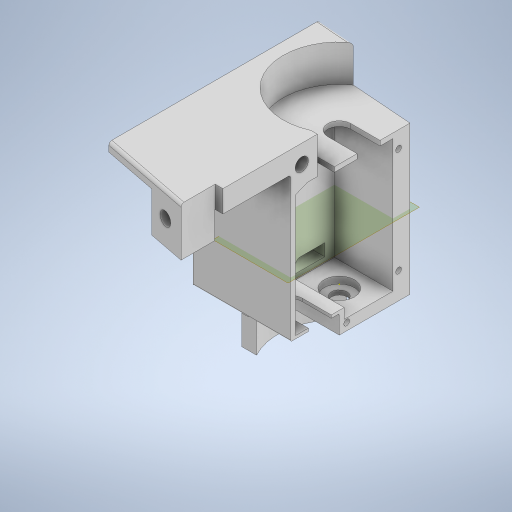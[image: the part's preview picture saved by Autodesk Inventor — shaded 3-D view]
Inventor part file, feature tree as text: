
AUTODESK INVENTOR PART (.ipt)
format: ipt  version: 2023.5 (Build 275446000, 446)  size: 1,221,120 bytes
history: native  units: mm
features: sketch x70, extrude x63, projected_geometry x47, reference x33, other x16, fillet x16, hole x6
ambient origin geometry x8: Origin, YZ Plane, XZ Plane, XY Plane, X Axis, Y Axis, Z Axis, Center Point
bodies: Body1 (feature_tree), Body2 (feature_tree)
feature tree (251):
  other  "Bryła1"
  extrude  "Wyciągnięcie proste1"  Depth=3.2mm
  extrude  "Wyciągnięcie proste2"  Depth=6.0mm
  extrude  "Wyciągnięcie proste3"  Depth=6.0mm
  extrude  "Wyciągnięcie proste4"  Depth=1.0mm TaperAngle=0.0deg
  extrude  "Wyciągnięcie proste5"  Depth=5.7mm
  extrude  "Wyciągnięcie proste6"  Depth=2.0mm TaperAngle=0.0deg
  extrude  "Wyciągnięcie proste7"  Depth=1.0mm TaperAngle=0.0deg
  extrude  "Wyciągnięcie proste8"  Depth=3.5mm
  extrude  "Wyciągnięcie proste9"  Depth=2.0mm TaperAngle=0.0deg
  extrude  "Wyciągnięcie proste10"  Depth=2.0mm TaperAngle=0.0deg
  extrude  "Wyciągnięcie proste11"  Depth=10.0mm TaperAngle=0.0deg
  extrude  "Wyciągnięcie proste12"  Depth=1.0mm
  extrude  "Wyciągnięcie proste13"  Depth=10.0mm TaperAngle=0.0deg
  extrude  "Wyciągnięcie proste14"  Depth=10.0mm TaperAngle=0.0deg
  extrude  "Wyciągnięcie proste15"  Depth=0.5mm
  extrude  "Wyciągnięcie proste16"  Depth=10.0mm TaperAngle=0.0deg
  sketch  "Szkic17"
  hole  "Otwór1"  [1 undecoded]
  other  "Płaszczyzna konstrukcyjna1"
  hole  "Otwór3"  [1 undecoded]
  extrude  "Wyciągnięcie proste18"  Depth=10.0mm TaperAngle=0.0deg
  extrude  "Wyciągnięcie proste19"  Depth=10.0mm TaperAngle=0.0deg
  hole  "Otwór4"  [1 undecoded]
  sketch  "Szkic24"
  other  "Płaszczyzna konstrukcyjna2"
  other  "Płaszczyzna konstrukcyjna3"
  extrude  "Wyciągnięcie proste20"  Depth=0.4mm
  extrude  "Wyciągnięcie proste21"  Depth=0.6mm TaperAngle=0.0deg
  extrude  "Wyciągnięcie proste22"  Depth=0.4mm
  fillet  "Zaokrąglenie1"  Radius=2.0mm
  extrude  "Wyciągnięcie proste23"  Depth=1.0mm TaperAngle=0.0deg
  extrude  "Wyciągnięcie proste24"  Depth=1.0mm TaperAngle=0.0deg
  extrude  "Wyciągnięcie proste25"  Depth=0.5mm
  extrude  "Wyciągnięcie proste26"  Depth=2.75mm
  extrude  "Wyciągnięcie proste27"  Depth=3.0mm
  extrude  "Wyciągnięcie proste28"  Depth=3.0mm
  extrude  "Wyciągnięcie proste29"  Depth=10.0mm TaperAngle=0.0deg
  extrude  "Wyciągnięcie proste30"  Depth=1.0mm
  extrude  "Wyciągnięcie proste31"  Depth=10.0mm
  hole  "Otwór5"  [1 undecoded]
  extrude  "Wyciągnięcie proste32"  Depth=2.75mm
  extrude  "Wyciągnięcie proste33"  Depth=2.75mm
  sketch  "Szkic40"
  sketch  "Szkic41"
  extrude  "Wyciągnięcie proste34"  Depth=10.0mm TaperAngle=0.0deg
  extrude  "Wyciągnięcie proste35"  Depth=10.0mm TaperAngle=0.0deg
  extrude  "Wyciągnięcie proste36"  Depth=4.0mm TaperAngle=0.0deg
  extrude  "Wyciągnięcie proste37"  Depth=5.0mm
  extrude  "Wyciągnięcie proste38"  Depth=4.0mm TaperAngle=0.0deg
  fillet  "Zaokrąglenie3"  Radius=10.0mm
  fillet  "Zaokrąglenie4"  Radius=10.0mm
  extrude  "Wyciągnięcie proste39"  Depth=5.0mm TaperAngle=0.0deg
  extrude  "Wyciągnięcie proste40"  Depth=1.8mm TaperAngle=0.0deg
  fillet  "Zaokrąglenie5"  Radius=1.8mm
  extrude  "Wyciągnięcie proste41"  Depth=10.0mm TaperAngle=0.0deg
  extrude  "Wyciągnięcie proste42"  Depth=10.0mm TaperAngle=0.0deg
  extrude  "Wyciągnięcie proste43"  Depth=1.0mm TaperAngle=0.0deg
  extrude  "Wyciągnięcie proste44"  Depth=3.5mm
  sketch  "Szkic51"
  extrude  "Wyciągnięcie proste45"  Depth=2.3mm
  extrude  "Wyciągnięcie proste46"  Depth=1.0mm TaperAngle=0.0deg
  extrude  "Wyciągnięcie proste47"  TaperAngle=0.0deg  [1 undecoded]
  extrude  "Wyciągnięcie proste48"  Depth=0.5mm
  extrude  "Wyciągnięcie proste49"  Depth=0.5mm
  fillet  "Zaokrąglenie6"  Radius=4.0mm
  extrude  "Wyciągnięcie proste50"  Depth=0.5mm
  extrude  "Wyciągnięcie proste51"  Depth=0.5mm
  fillet  "Zaokrąglenie7"  Radius=0.5mm
  extrude  "Wyciągnięcie proste52"  Depth=0.5mm
  fillet  "Zaokrąglenie8"  Radius=0.5mm
  fillet  "Zaokrąglenie9"  Radius=0.2mm
  extrude  "Wyciągnięcie proste53"  Depth=2.0mm TaperAngle=0.0deg
  extrude  "Wyciągnięcie proste54"  Depth=2.0mm TaperAngle=0.0deg
  fillet  "Zaokrąglenie10"  Radius=10.0mm
  extrude  "Wyciągnięcie proste55"  Depth=10.0mm TaperAngle=0.0deg
  fillet  "Zaokrąglenie12"  Radius=2.0mm
  hole  "Otwór6"  [1 undecoded]
  extrude  "Wyciągnięcie proste56"  TaperAngle=0.0deg  [1 undecoded]
  hole  "Otwór7"  [1 undecoded]
  extrude  "Wyciągnięcie proste57"  Depth=1.0mm
  extrude  "Wyciągnięcie proste58"  Depth=2.0mm TaperAngle=0.0deg
  extrude  "Wyciągnięcie proste59"  Depth=2.0mm TaperAngle=0.0deg
  sketch  "Szkic67"
  extrude  "Wyciągnięcie proste60"  Depth=10.0mm TaperAngle=0.0deg
  extrude  "Wyciągnięcie proste61"  Depth=10.0mm TaperAngle=0.0deg
  extrude  "Wyciągnięcie proste62"  Depth=15.0mm TaperAngle=0.0deg
  fillet  "Zaokrąglenie13"  Radius=10.0mm
  fillet  "Zaokrąglenie14"  Radius=0.5mm
  fillet  "Zaokrąglenie15"  Radius=0.5mm
  fillet  "Zaokrąglenie16"  Radius=10.0mm
  extrude  "Wyciągnięcie proste63"  Depth=2.0mm
  fillet  "Zaokrąglenie17"  Radius=10.0mm
  fillet  "Zaokrąglenie18"  Radius=10.0mm
  extrude  "Wyciągnięcie proste64"  Depth=40.0mm
  sketch  "Szkic1"
  sketch  "Szkic2"
  projected_geometry  "Pętla rzutowana1"
  sketch  "Szkic3"
  projected_geometry  "Pętla rzutowana2"
  sketch  "Szkic4"
  reference  "Odniesienie1"
  reference  "Odniesienie2"
  projected_geometry  "Pętla rzutowana3"
  reference  "Odniesienie3"
  reference  "Odniesienie4"
  reference  "Odniesienie5"
  sketch  "Szkic5"
  reference  "Odniesienie6"
  reference  "Odniesienie7"
  sketch  "Szkic6"
  reference  "Odniesienie8"
  sketch  "Szkic7"
  projected_geometry  "Pętla rzutowana4"
  sketch  "Szkic8"
  sketch  "Szkic9"
  reference  "Odniesienie9"
  sketch  "Szkic10"
  reference  "Odniesienie10"
  projected_geometry  "Pętla rzutowana5"
  sketch  "Szkic11"
  reference  "Odniesienie11"
  projected_geometry  "Pętla rzutowana6"
  sketch  "Szkic12"
  sketch  "Szkic13"
  projected_geometry  "Pętla rzutowana7"
  sketch  "Szkic14"
  reference  "Odniesienie12"
  reference  "Odniesienie13"
  sketch  "Szkic15"
  reference  "Odniesienie14"
  reference  "Odniesienie15"
  reference  "Odniesienie16"
  sketch  "Szkic16"
  projected_geometry  "Pętla rzutowana8"
  reference  "Odniesienie17"
  reference  "Odniesienie18"
  sketch  "Szkic18"
  projected_geometry  "Pętla rzutowana9"
  sketch  "Szkic20"
  projected_geometry  "Pętla rzutowana10"
  sketch  "Szkic21"
  reference  "Odniesienie19"
  reference  "Odniesienie20"
  reference  "Odniesienie21"
  reference  "Odniesienie22"
  sketch  "Szkic22"
  reference  "Odniesienie23"
  reference  "Odniesienie24"
  sketch  "Szkic23"
  projected_geometry  "Pętla rzutowana11"
  reference  "Odniesienie25"
  sketch  "Szkic26"
  projected_geometry  "Pętla rzutowana12"
  sketch  "Szkic27"
  reference  "Odniesienie26"
  reference  "Odniesienie27"
  sketch  "Szkic28"
  projected_geometry  "Pętla rzutowana13"
  sketch  "Szkic29"
  projected_geometry  "Pętla rzutowana14"
  sketch  "Szkic30"
  sketch  "Szkic31"
  projected_geometry  "Pętla rzutowana15"
  reference  "Odniesienie28"
  reference  "Odniesienie29"
  sketch  "Szkic32"
  reference  "Odniesienie30"
  reference  "Odniesienie31"
  sketch  "Szkic33"
  projected_geometry  "Pętla rzutowana16"
  sketch  "Szkic34"
  projected_geometry  "Pętla rzutowana17"
  sketch  "Szkic35"
  projected_geometry  "Pętla rzutowana18"
  sketch  "Szkic36"
  projected_geometry  "Pętla rzutowana19"
  sketch  "Szkic37"
  projected_geometry  "Pętla rzutowana20"
  sketch  "Szkic38"
  sketch  "Szkic39"
  projected_geometry  "Pętla rzutowana21"
  reference  "Odniesienie32"
  reference  "Odniesienie33"
  sketch  "Szkic42"
  projected_geometry  "Pętla rzutowana22"
  sketch  "Szkic43"
  projected_geometry  "Pętla rzutowana23"
  projected_geometry  "Pętla rzutowana24"
  sketch  "Szkic44"
  projected_geometry  "Pętla rzutowana25"
  projected_geometry  "Pętla rzutowana26"
  sketch  "Szkic45"
  projected_geometry  "Pętla rzutowana27"
  sketch  "Szkic46"
  projected_geometry  "Pętla rzutowana28"
  sketch  "Szkic47"
  sketch  "Szkic48"
  sketch  "Szkic49"
  projected_geometry  "Pętla rzutowana29"
  sketch  "Szkic50"
  projected_geometry  "Pętla rzutowana30"
  projected_geometry  "Pętla rzutowana31"
  projected_geometry  "Pętla rzutowana32"
  sketch  "Szkic52"
  sketch  "Szkic53"
  projected_geometry  "Pętla rzutowana33"
  sketch  "Szkic54"
  projected_geometry  "Pętla rzutowana34"
  sketch  "Szkic55"
  projected_geometry  "Pętla rzutowana35"
  sketch  "Szkic56"
  sketch  "Szkic57"
  projected_geometry  "Pętla rzutowana36"
  sketch  "Szkic58"
  projected_geometry  "Pętla rzutowana37"
  sketch  "Szkic59"
  projected_geometry  "Pętla rzutowana38"
  projected_geometry  "Pętla rzutowana39"
  sketch  "Szkic60"
  projected_geometry  "Pętla rzutowana40"
  sketch  "Szkic61"
  projected_geometry  "Pętla rzutowana41"
  sketch  "Szkic62"
  projected_geometry  "Pętla rzutowana42"
  sketch  "Szkic63"
  projected_geometry  "Pętla rzutowana43"
  sketch  "Szkic64"
  sketch  "Szkic65"
  sketch  "Szkic66"
  projected_geometry  "Pętla rzutowana44"
  sketch  "Szkic68"
  projected_geometry  "Pętla rzutowana45"
  sketch  "Szkic69"
  projected_geometry  "Pętla rzutowana46"
  sketch  "Szkic70"
  projected_geometry  "Pętla rzutowana47"
  sketch  "Szkic71"
  sketch  "Szkic72"
  parser-record x1  (decoder bookkeeping rows leaked as tree rows — omitted from the tree; the rows remain in map.json)
  other  "stratos_v2_mechanics.iam"
  other  "silnik:2"
  other  "silnik:1"
  other  "lipo-300:1"
  other  "podstawa_v2:1"
  other  "kolo:1"
  other  "kolo:2"
  other  "wymiar:1"
  other  "MikroSumo:1"
  other  "nozzyk:1"
  other  "scianka_prawa:1"
note: 8 required parameter values undecoded (feature->parameter linkage not recoverable at this tier; creation-order binding heuristic only, values carry confidence <= 0.55)
note: 1 file-system path scrubbed to <path> (originals preserved in map.json)
